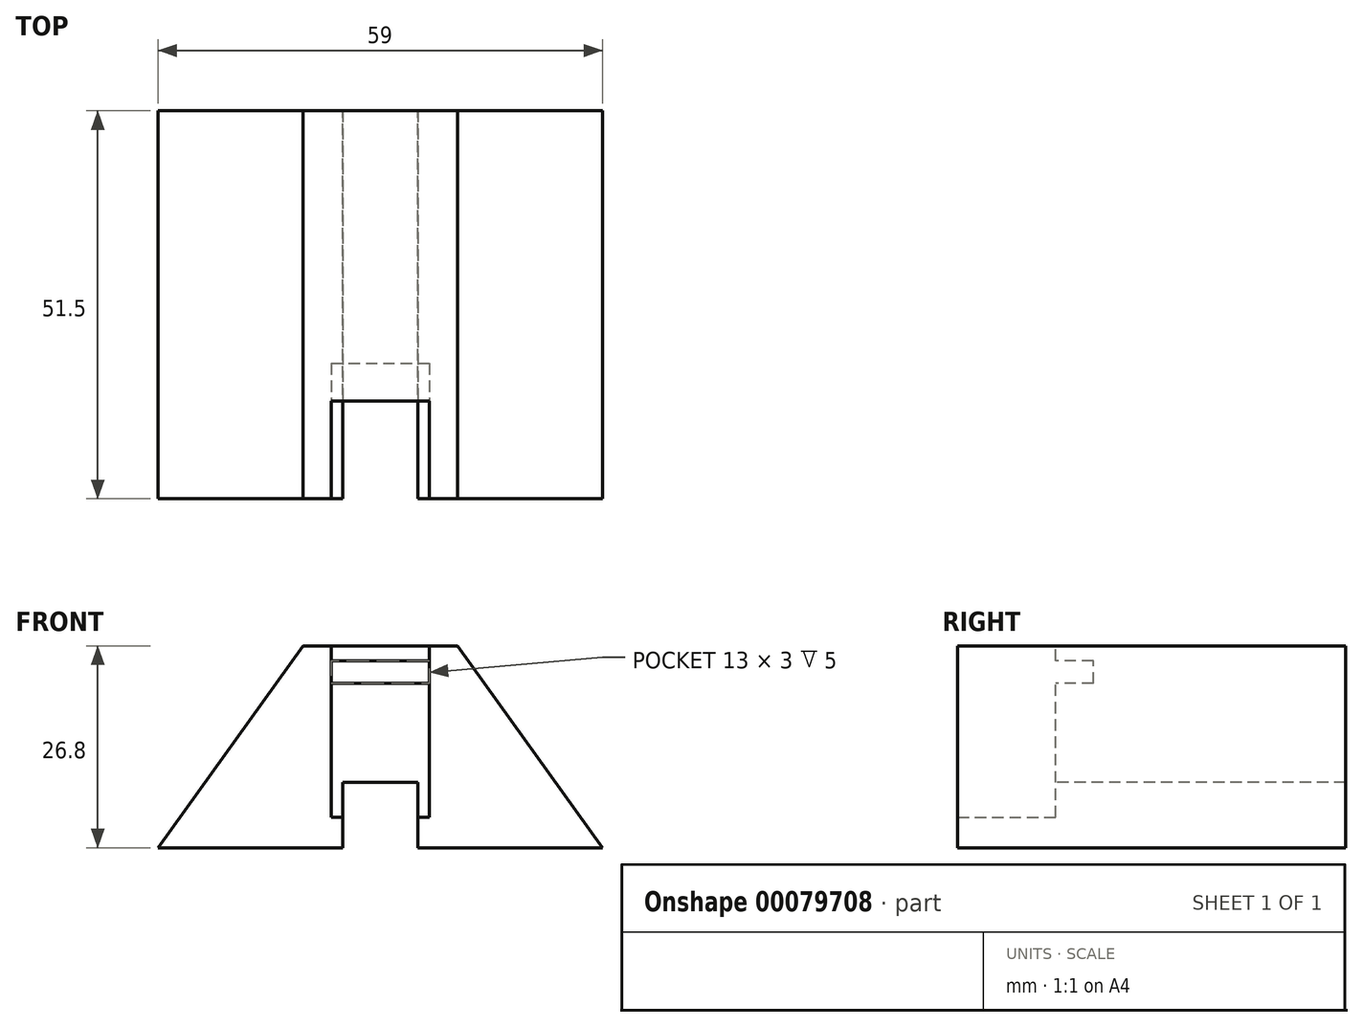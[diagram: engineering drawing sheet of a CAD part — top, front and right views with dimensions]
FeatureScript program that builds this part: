
annotation { "Feature Type Name" : "Feature", "Feature Type Description" : "" }
export const myFeature = defineFeature(function(context is Context, id is Id, definition is map)
    precondition{}
    {
        {
            var Q0;
            Q0=qCreatedBy(makeId("Top.planeOp"),FACE);
            var sketch = newSketch(context, id + "F0", { "sketchPlane" : qUnion([Q0])});
            skLineSegment(sketch, "E0.bottom", {"start": v(-29.5, 51.5) * mm, "end": v(29.5, 51.5) * mm});
            skLineSegment(sketch, "E0.top", {"start": v(-29.5, 0) * mm, "end": v(-5, 0) * mm});
            skLineSegment(sketch, "E0.left", {"start": v(-29.5, 51.5) * mm, "end": v(-29.5, 0) * mm});
            skLineSegment(sketch, "E0.right", {"start": v(29.5, 51.5) * mm, "end": v(29.5, 0) * mm});
            skLineSegment(sketch, "E1", {"start": v(-5, 0) * mm, "end": v(-5, 13) * mm});
            skLineSegment(sketch, "E2", {"start": v(5, 0) * mm, "end": v(5, 13) * mm});
            skLineSegment(sketch, "E3", {"start": v(-5, 13) * mm, "end": v(5, 13) * mm});
            skLineSegment(sketch, "E4.trimOffspring", {"start": v(5, 0) * mm, "end": v(29.5, 0) * mm});
            skSolve(sketch);
        }
        {
            var Q0;
            Q0 = qSketchRegion(id + "F0", true);
            extrude(context, id + "F1", {"entities" : qUnion([Q0]), "depth" : 26.8 * mm});
        }
        {
            var Q0;
            Q0=makeQuery(id+"F1.opExtrude","SWEPT_FACE",FACE,{"disambiguationData":[OSD([sQuery(id+"F0.wireOp",EDGE,"E0.top")])]});
            var sketch = newSketch(context, id + "F2", { "sketchPlane" : qUnion([Q0])});
            skLineSegment(sketch, "E5", {"start": v(-29.5, 0) * mm, "end": v(-10.24, 26.8) * mm});
            skLineSegment(sketch, "E6", {"start": v(-10.24, 26.8) * mm, "end": v(-29.5, 26.8) * mm});
            skLineSegment(sketch, "E7", {"start": v(-29.5, 26.8) * mm, "end": v(-29.5, 0) * mm});
            skLineSegment(sketch, "E8", {"start": v(29.5, 0) * mm, "end": v(10.24, 26.8) * mm});
            skPoint(sketch, "E8.startSnap0", {"position": v(-17.25, 0) * mm});
            skLineSegment(sketch, "E9", {"start": v(10.24, 26.8) * mm, "end": v(29.5, 26.8) * mm});
            skLineSegment(sketch, "E10", {"start": v(29.5, 26.8) * mm, "end": v(29.5, 0) * mm});
            skSolve(sketch);
        }
        {
            var Q0;
            Q0=makeQuery(id+"F2.imprint","IMPRINT",FACE,{"disambiguationData":[TD([[makeQuery(id+"F2.imprint","IMPRINT",EDGE,{"derivedFrom":sQuery(id+"F2.wireOp",EDGE,"E8")}),-1.0]])]});
            var Q1;
            Q1=makeQuery(id+"F2.imprint","IMPRINT",FACE,{"disambiguationData":[TD([[makeQuery(id+"F2.imprint","IMPRINT",EDGE,{"derivedFrom":sQuery(id+"F2.wireOp",EDGE,"E5")}),1.0]])]});
            var Q2;
            Q2=makeQuery(id+"F1.opExtrude","SWEPT_FACE",FACE,{"disambiguationData":[OSD([sQuery(id+"F0.wireOp",EDGE,"E0.bottom")])]});
            extrude(context, id + "F3", {"entities" : qUnion([Q0, Q1]), "operationType" : NewBodyOperationType.REMOVE, "endBound" : BoundingType.UP_TO_SURFACE, "oppositeDirection" : true, "endBoundEntityFace" : qUnion([Q2]), "depth" : 25 * mm});
        }
        {
            var Q0;
            Q0=makeQuery(id+"F1.opExtrude","SWEPT_FACE",FACE,{"disambiguationData":[OSD([sQuery(id+"F0.wireOp",EDGE,"E3")])]});
            var sketch = newSketch(context, id + "F4", { "sketchPlane" : qUnion([Q0])});
            skLineSegment(sketch, "E11", {"start": v(-6.5, 24.8) * mm, "end": v(6.5, 24.8) * mm});
            skLineSegment(sketch, "E12", {"start": v(6.5, 24.8) * mm, "end": v(6.5, 21.8) * mm});
            skLineSegment(sketch, "E13", {"start": v(6.5, 21.8) * mm, "end": v(-6.5, 21.8) * mm});
            skLineSegment(sketch, "E14", {"start": v(-6.5, 21.8) * mm, "end": v(-6.5, 24.8) * mm});
            skSolve(sketch);
        }
        {
            var Q0;
            Q0 = qSketchRegion(id + "F4", true);
            extrude(context, id + "F5", {"entities" : qUnion([Q0]), "operationType" : NewBodyOperationType.REMOVE, "oppositeDirection" : true, "depth" : 5 * mm});
        }
        {
            var Q0;
            Q0=makeQuery(id+"F1.opExtrude","CAP_FACE",FACE,{"disambiguationData":[OSD([sQuery(id+"F0.wireOp",EDGE,"E0.bottom"),sQuery(id+"F0.wireOp",EDGE,"E0.top"),sQuery(id+"F0.wireOp",EDGE,"E0.left"),sQuery(id+"F0.wireOp",EDGE,"E0.right"),sQuery(id+"F0.wireOp",EDGE,"E1"),sQuery(id+"F0.wireOp",EDGE,"E2"),sQuery(id+"F0.wireOp",EDGE,"E3"),sQuery(id+"F0.wireOp",EDGE,"E4.trimOffspring")])],"isStart":false});
            var sketch = newSketch(context, id + "F6", { "sketchPlane" : qUnion([Q0])});
            skLineSegment(sketch, "E15", {"start": v(-6.5, 13) * mm, "end": v(-6.5, 0) * mm});
            skLineSegment(sketch, "E16", {"start": v(6.5, 13) * mm, "end": v(6.5, 0) * mm});
            skLineSegment(sketch, "E17", {"start": v(-6.5, 13) * mm, "end": v(-5, 13) * mm});
            skLineSegment(sketch, "E18", {"start": v(6.5, 13) * mm, "end": v(5, 13) * mm});
            skLineSegment(sketch, "E19", {"start": v(5, 13) * mm, "end": v(5, 0) * mm});
            skLineSegment(sketch, "E20", {"start": v(5, 0) * mm, "end": v(6.5, 0) * mm});
            skLineSegment(sketch, "E21", {"start": v(-5, 13) * mm, "end": v(-5, 0) * mm});
            skLineSegment(sketch, "E22", {"start": v(-5, 0) * mm, "end": v(-6.5, 0) * mm});
            skSolve(sketch);
        }
        {
            var Q0;
            Q0 = qSketchRegion(id + "F6", true);
            extrude(context, id + "F7", {"entities" : qUnion([Q0]), "operationType" : NewBodyOperationType.REMOVE, "oppositeDirection" : true, "depth" : 22.75 * mm});
        }
        {
            var Q0;
            {var subQ0=sQuery(id+"F4.wireOp",EDGE,"E13");var subQ3=sQuery(id+"F0.wireOp",EDGE,"E3");Q0=makeQuery(id+"F7.boolean.opBoolean","MERGE",FACE,{"derivedFrom":[makeQuery(id+"F5.boolean.opBoolean","SPLIT",FACE,{"disambiguationData":[TD([makeQuery(id+"F5.opExtrude","SWEPT_FACE",FACE,{"disambiguationData":[OSD([subQ0])]})])],"derivedFrom":makeQuery(id+"F1.opExtrude","SWEPT_FACE",FACE,{"disambiguationData":[OSD([subQ3])]})}),makeQuery(id+"F7.opExtrude","SWEPT_FACE",FACE,{"disambiguationData":[OSD([sQuery(id+"F6.wireOp",EDGE,"E17")])]}),makeQuery(id+"F7.opExtrude","SWEPT_FACE",FACE,{"disambiguationData":[OSD([sQuery(id+"F6.wireOp",EDGE,"E18")])]})]});}
            var sketch = newSketch(context, id + "F8", { "sketchPlane" : qUnion([Q0])});
            skLineSegment(sketch, "E23", {"start": v(-5, 0) * mm, "end": v(-5, 8.7) * mm});
            skLineSegment(sketch, "E24", {"start": v(5, 0) * mm, "end": v(5, 8.7) * mm});
            skLineSegment(sketch, "E25", {"start": v(5, 8.7) * mm, "end": v(-5, 8.7) * mm});
            skLineSegment(sketch, "E26", {"start": v(-5, 0) * mm, "end": v(5, 0) * mm});
            skSolve(sketch);
        }
        {
            var Q0;
            Q0 = qSketchRegion(id + "F8", true);
            var Q1;
            Q1=makeQuery(id+"F1.opExtrude","SWEPT_FACE",FACE,{"disambiguationData":[OSD([sQuery(id+"F0.wireOp",EDGE,"E0.bottom")])]});
            extrude(context, id + "F9", {"entities" : qUnion([Q0]), "operationType" : NewBodyOperationType.REMOVE, "endBound" : BoundingType.UP_TO_SURFACE, "oppositeDirection" : true, "endBoundEntityFace" : qUnion([Q1]), "depth" : 25 * mm});
        }
    });
